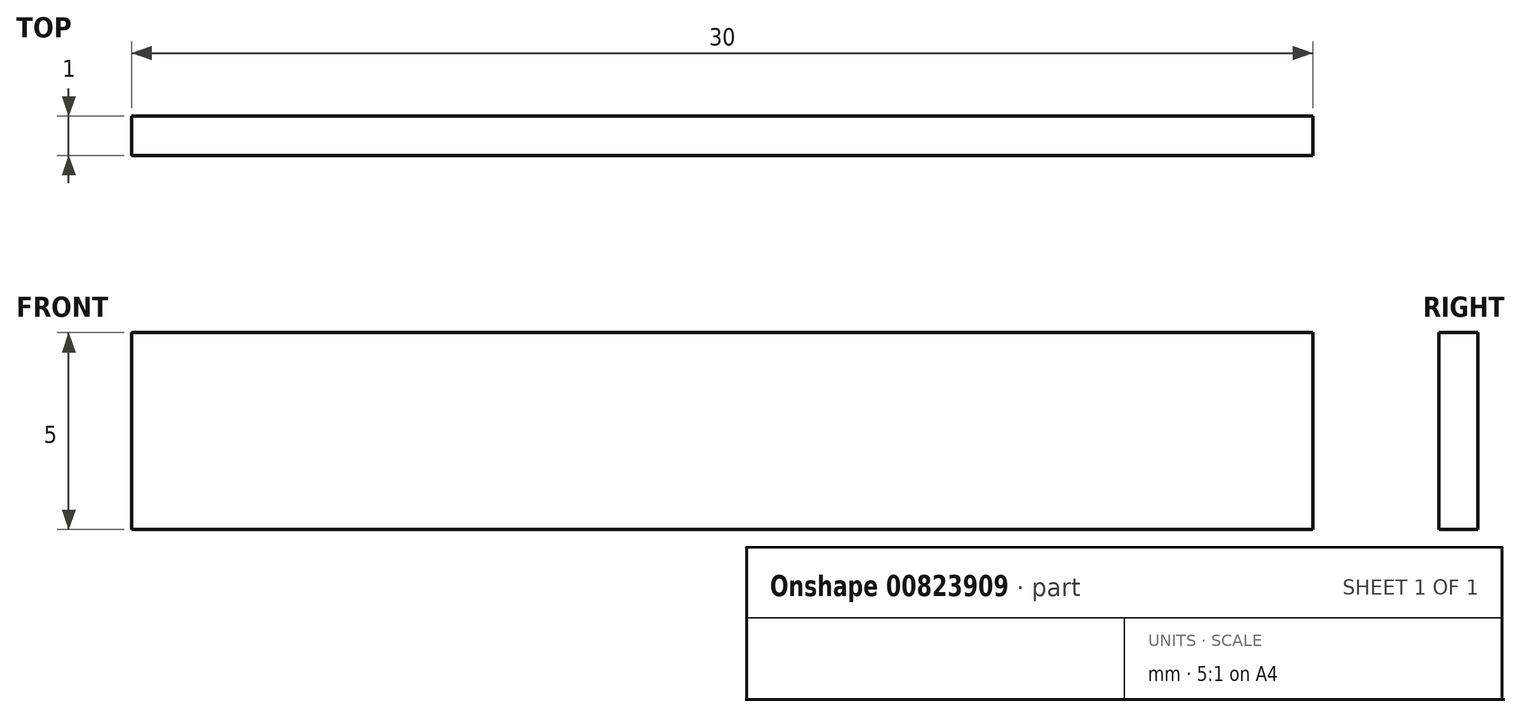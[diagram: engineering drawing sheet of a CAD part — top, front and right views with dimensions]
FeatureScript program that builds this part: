
annotation { "Feature Type Name" : "Feature", "Feature Type Description" : "" }
export const myFeature = defineFeature(function(context is Context, id is Id, definition is map)
    precondition{}
    {
        {
            var Q0;
            Q0=qCreatedBy(makeId("Top.planeOp"),FACE);
            var sketch = newSketch(context, id + "F0", { "sketchPlane" : qUnion([Q0])});
            skLineSegment(sketch, "E0.bottom", {"start": v(-30, 0) * mm, "end": v(0, 0) * mm});
            skLineSegment(sketch, "E0.top", {"start": v(-30, -1) * mm, "end": v(0, -1) * mm});
            skLineSegment(sketch, "E0.left", {"start": v(-30, 0) * mm, "end": v(-30, -1) * mm});
            skLineSegment(sketch, "E0.right", {"start": v(0, 0) * mm, "end": v(0, -1) * mm});
            skSolve(sketch);
        }
        {
            var Q0;
            Q0 = qSketchRegion(id + "F0", true);
            extrude(context, id + "F1", {"entities" : qUnion([Q0]), "depth" : 5 * mm, "offsetDistance" : 25 * mm});
        }
    });
